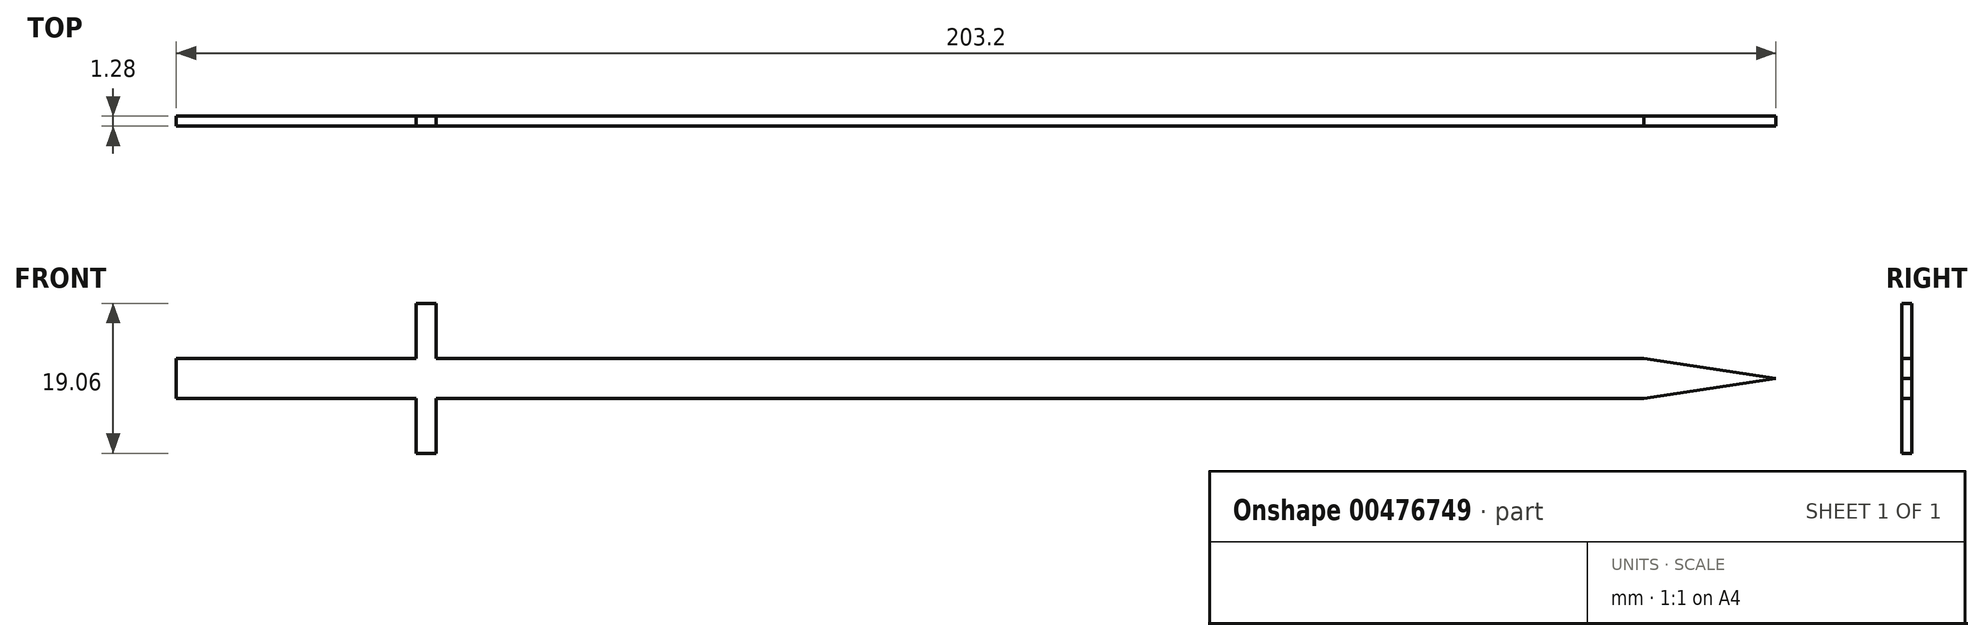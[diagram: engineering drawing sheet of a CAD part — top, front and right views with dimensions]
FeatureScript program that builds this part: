
annotation { "Feature Type Name" : "Feature", "Feature Type Description" : "" }
export const myFeature = defineFeature(function(context is Context, id is Id, definition is map)
    precondition{}
    {
        {
            var Q0;
            Q0=qCreatedBy(makeId("Front.planeOp"),FACE);
            var sketch = newSketch(context, id + "F0", { "sketchPlane" : qUnion([Q0])});
            skLineSegment(sketch, "E0", {"start": v(-111.92, -9.53) * mm, "end": v(-111.92, 9.52) * mm});
            skLineSegment(sketch, "E1.0", {"start": v(-142.4, -2.54) * mm, "end": v(44, -2.54) * mm});
            skLineSegment(sketch, "E2.0", {"start": v(-142.4, 2.54) * mm, "end": v(44, 2.54) * mm});
            skLineSegment(sketch, "E3.0", {"start": v(-109.38, -9.53) * mm, "end": v(-109.38, 9.53) * mm});
            skLineSegment(sketch, "E4", {"start": v(-109.38, 9.53) * mm, "end": v(-111.92, 9.52) * mm});
            skLineSegment(sketch, "E5", {"start": v(-109.38, -9.53) * mm, "end": v(-111.92, -9.53) * mm});
            skLineSegment(sketch, "E6", {"start": v(-142.4, -2.54) * mm, "end": v(-142.4, 2.54) * mm});
            skLineSegment(sketch, "E7", {"start": v(44, 2.54) * mm, "end": v(60.8, 0) * mm});
            skLineSegment(sketch, "E8", {"start": v(44, -2.54) * mm, "end": v(60.8, 0) * mm});
            skPoint(sketch, "E9.orphan", {"position": v(-142.4, 0) * mm});
            skSolve(sketch);
        }
        {
            var Q0;
            {var subQ0=sQuery(id+"F0.wireOp",EDGE,"E7");Q0=makeQuery(id+"F0.imprint","IMPRINT",FACE,{"disambiguationData":[TD([[makeQuery(id+"F0.imprint","IMPRINT",EDGE,{"derivedFrom":subQ0}),-1.0]])]});}
            var Q1;
            {var subQ5=sQuery(id+"F0.wireOp",EDGE,"E6");Q1=makeQuery(id+"F0.imprint","IMPRINT",FACE,{"disambiguationData":[TD([[makeQuery(id+"F0.imprint","IMPRINT",EDGE,{"derivedFrom":subQ5}),-1.0]])]});}
            var Q2;
            {var subQ0=sQuery(id+"F0.wireOp",EDGE,"E1.0");var subQ1=sQuery(id+"F0.wireOp",EDGE,"E0");var subQ2=makeQuery(id+"F0.imprint","INTERSECT",VERTEX,{"derivedFrom":[subQ1,subQ0]});Q2=makeQuery(id+"F0.imprint","IMPRINT",FACE,{"disambiguationData":[TD([[makeQuery(id+"F0.imprint","IMPRINT",EDGE,{"disambiguationData":[TD([[subQ2,-1.0]])],"derivedFrom":subQ1}),-1.0]])]});}
            extrude(context, id + "F1", {"entities" : qUnion([Q0, Q1, Q2]), "endBound" : BoundingType.SYMMETRIC, "depth" : 1.27 * mm});
        }
        {
            var Q0;
            {var subQ0=sQuery(id+"F0.wireOp",EDGE,"E4");Q0=makeQuery(id+"F0.imprint","IMPRINT",FACE,{"disambiguationData":[TD([[makeQuery(id+"F0.imprint","IMPRINT",EDGE,{"derivedFrom":subQ0}),1.0]])]});}
            var Q1;
            {var subQ0=sQuery(id+"F0.wireOp",EDGE,"E5");Q1=makeQuery(id+"F0.imprint","IMPRINT",FACE,{"disambiguationData":[TD([[makeQuery(id+"F0.imprint","IMPRINT",EDGE,{"derivedFrom":subQ0}),-1.0]])]});}
            extrude(context, id + "F2", {"entities" : qUnion([Q0, Q1]), "operationType" : NewBodyOperationType.ADD, "endBound" : BoundingType.SYMMETRIC, "depth" : 1.27 * mm});
        }
    });
